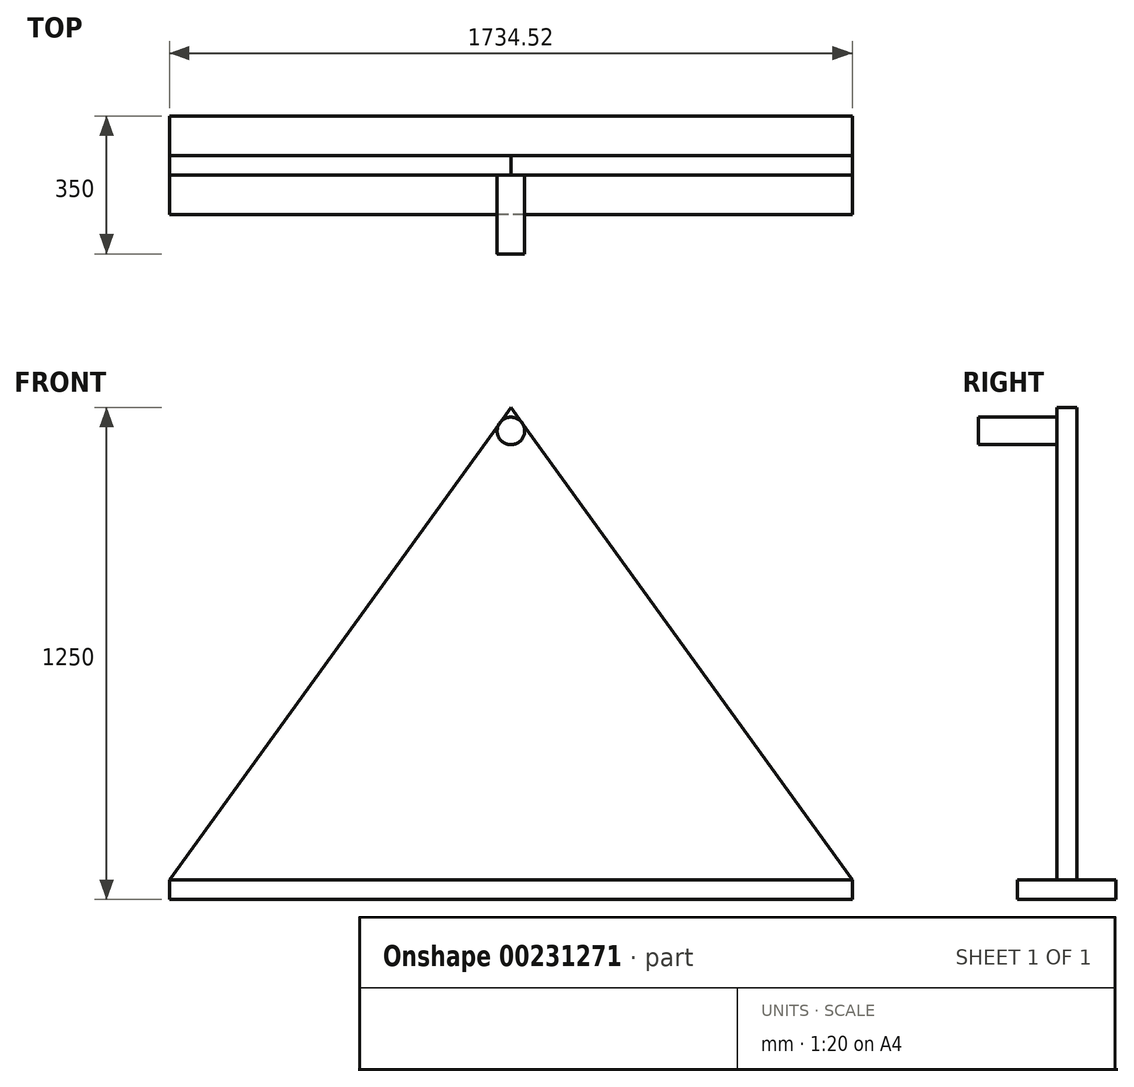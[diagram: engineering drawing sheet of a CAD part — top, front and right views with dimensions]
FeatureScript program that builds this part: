
annotation { "Feature Type Name" : "Feature", "Feature Type Description" : "" }
export const myFeature = defineFeature(function(context is Context, id is Id, definition is map)
    precondition{}
    {
        {
            var Q0;
            Q0=qCreatedBy(makeId("Front.planeOp"),FACE);
            var sketch = newSketch(context, id + "F0", { "sketchPlane" : qUnion([Q0])});
            skLineSegment(sketch, "E0", {"start": v(-867.26, 0) * mm, "end": v(867.26, 0) * mm});
            skLineSegment(sketch, "E1", {"start": v(867.26, 0) * mm, "end": v(0, 1200) * mm});
            skLineSegment(sketch, "E2", {"start": v(0, 1200) * mm, "end": v(-867.26, 0) * mm});
            skLineSegment(sketch, "E3", {"start": v(0, 1200) * mm, "end": v(0, 0) * mm, "construction": true});
            skSolve(sketch);
        }
        {
            var Q0;
            Q0=makeQuery(id+"F0.imprint","IMPRINT",FACE,{"disambiguationData":[TD([[makeQuery(id+"F0.imprint","IMPRINT",EDGE,{"derivedFrom":sQuery(id+"F0.wireOp",EDGE,"E0")}),1.0]])]});
            extrude(context, id + "F1", {"entities" : qUnion([Q0]), "endBound" : BoundingType.SYMMETRIC, "depth" : 50 * mm});
        }
        {
            var Q0;
            Q0=makeQuery(id+"F1.opExtrude","CAP_FACE",FACE,{"disambiguationData":[OSD([sQuery(id+"F0.wireOp",EDGE,"E0"),sQuery(id+"F0.wireOp",EDGE,"E1"),sQuery(id+"F0.wireOp",EDGE,"E2")])],"isStart":false});
            var sketch = newSketch(context, id + "F2", { "sketchPlane" : qUnion([Q0])});
            skCircle(sketch, "E4", {"center": v(0, 1140.25) * mm, "radius": 35 * mm});
            skSolve(sketch);
        }
        {
            var Q0;
            {var subQ0=sQuery(id+"F2.wireOp",EDGE,"E4");var subQ1=makeQuery(id+"F2.imprint","INTERSECT",VERTEX,{"derivedFrom":[makeQuery(id+"F1.opExtrude","CAP_EDGE",EDGE,{"disambiguationData":[OSD([sQuery(id+"F0.wireOp",EDGE,"E1")])],"isStart":false}),subQ0]});Q0=makeQuery(id+"F2.imprint","IMPRINT",FACE,{"disambiguationData":[TD([[makeQuery(id+"F2.imprint","IMPRINT",EDGE,{"disambiguationData":[TD([[subQ1,-1.0]])],"derivedFrom":subQ0}),1.0]])]});}
            extrude(context, id + "F3", {"entities" : qUnion([Q0]), "operationType" : NewBodyOperationType.ADD, "depth" : 200 * mm});
        }
        {
            var Q0;
            Q0=makeQuery(id+"F1.opExtrude","SWEPT_FACE",FACE,{"disambiguationData":[OSD([sQuery(id+"F0.wireOp",EDGE,"E0")])]});
            var sketch = newSketch(context, id + "F4", { "sketchPlane" : qUnion([Q0])});
            skLineSegment(sketch, "E5.bottom", {"start": v(867.26, 125) * mm, "end": v(-867.26, 125) * mm});
            skLineSegment(sketch, "E5.top", {"start": v(867.26, -125) * mm, "end": v(-867.26, -125) * mm});
            skLineSegment(sketch, "E5.left", {"start": v(867.26, 125) * mm, "end": v(867.26, -125) * mm});
            skLineSegment(sketch, "E5.right", {"start": v(-867.26, 125) * mm, "end": v(-867.26, -125) * mm});
            skPoint(sketch, "E5.middle", {"position": v(0, 0) * mm});
            skSolve(sketch);
        }
        {
            var Q0;
            {var subQ0=sQuery(id+"F4.wireOp",EDGE,"E5.bottom");Q0=makeQuery(id+"F4.imprint","IMPRINT",FACE,{"disambiguationData":[TD([[makeQuery(id+"F4.imprint","IMPRINT",EDGE,{"derivedFrom":subQ0}),1.0]])]});}
            var Q1;
            Q1=makeQuery(id+"F1.opExtrude","SWEPT_FACE",FACE,{"disambiguationData":[OSD([sQuery(id+"F0.wireOp",EDGE,"E0")])]});
            var Q2;
            {var subQ0=sQuery(id+"F4.wireOp",EDGE,"E5.top");Q2=makeQuery(id+"F4.imprint","IMPRINT",FACE,{"disambiguationData":[TD([[makeQuery(id+"F4.imprint","IMPRINT",EDGE,{"derivedFrom":subQ0}),-1.0]])]});}
            extrude(context, id + "F5", {"entities" : qUnion([Q0, Q1, Q2]), "operationType" : NewBodyOperationType.ADD, "depth" : 50 * mm});
        }
    });
